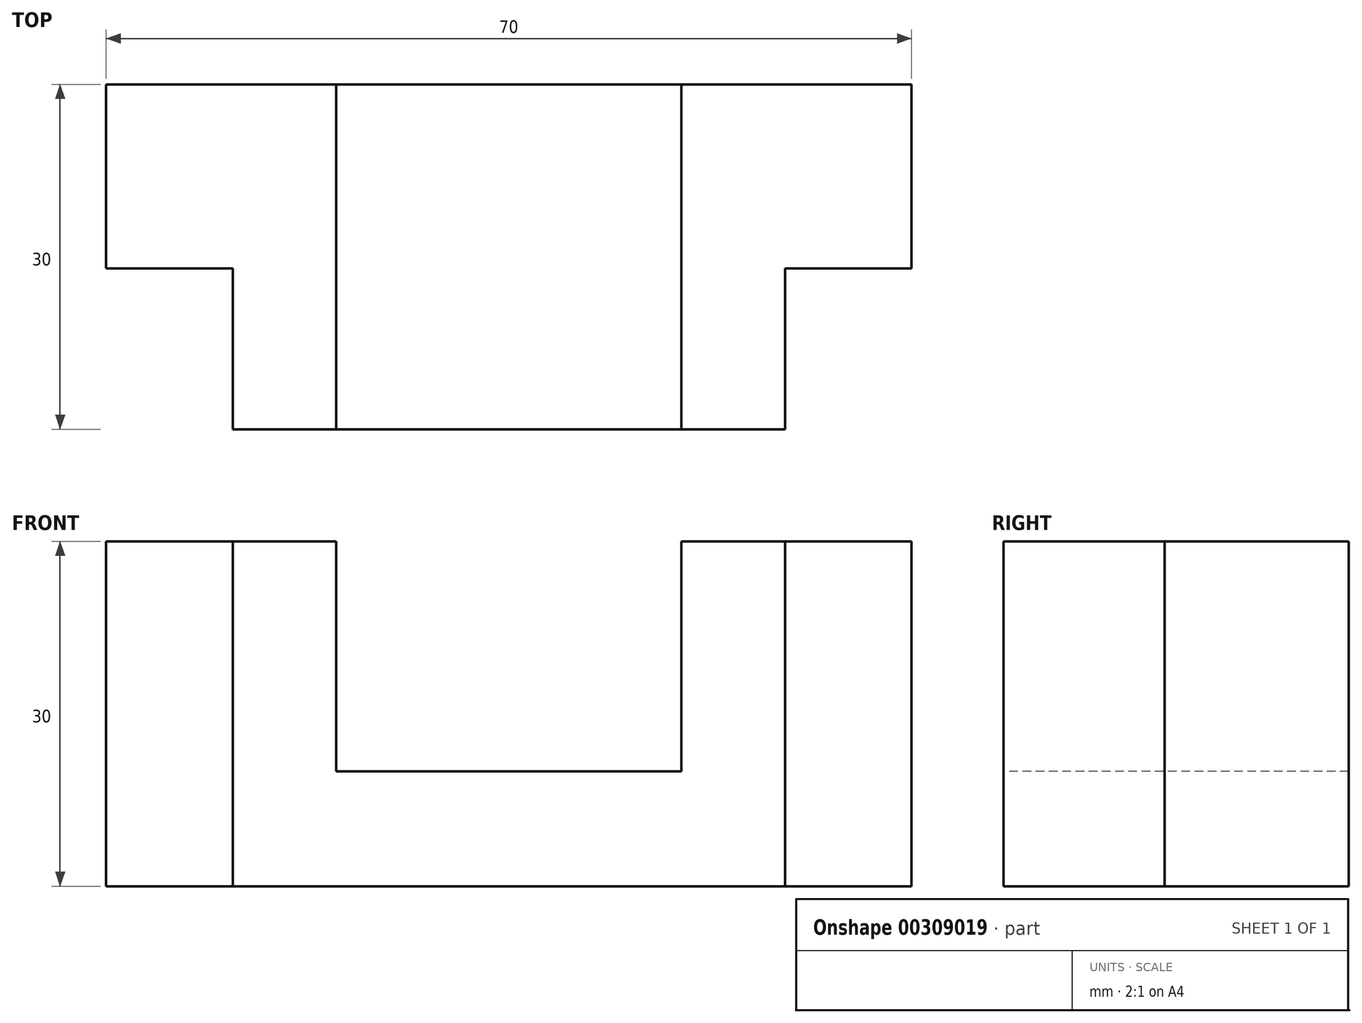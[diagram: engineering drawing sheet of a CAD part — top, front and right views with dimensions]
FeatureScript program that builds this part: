
annotation { "Feature Type Name" : "Feature", "Feature Type Description" : "" }
export const myFeature = defineFeature(function(context is Context, id is Id, definition is map)
    precondition{}
    {
        {
            var Q0;
            Q0=qCreatedBy(makeId("Top.planeOp"),FACE);
            var sketch = newSketch(context, id + "F0", { "sketchPlane" : qUnion([Q0])});
            skLineSegment(sketch, "E0", {"start": v(-35, 16) * mm, "end": v(-35, 0) * mm});
            skLineSegment(sketch, "E1", {"start": v(-24, -14) * mm, "end": v(24, -14) * mm});
            skLineSegment(sketch, "E2", {"start": v(35, 0) * mm, "end": v(35, 16) * mm});
            skLineSegment(sketch, "E3", {"start": v(35, 16) * mm, "end": v(-35, 16) * mm});
            skPoint(sketch, "E4.orphan", {"position": v(-35, 16.86) * mm});
            skLineSegment(sketch, "E5", {"start": v(-35, 0) * mm, "end": v(-24, 0) * mm});
            skLineSegment(sketch, "E6", {"start": v(-24, 0) * mm, "end": v(-24, -14) * mm});
            skLineSegment(sketch, "E7", {"start": v(35, 0) * mm, "end": v(24, 0) * mm});
            skLineSegment(sketch, "E8", {"start": v(24, 0) * mm, "end": v(24, -14) * mm});
            skPoint(sketch, "E9.orphan", {"position": v(-35, -14) * mm});
            skSolve(sketch);
        }
        {
            var Q0;
            Q0=makeQuery(id+"F0.imprint","IMPRINT",FACE,{"disambiguationData":[TD([[makeQuery(id+"F0.imprint","IMPRINT",EDGE,{"derivedFrom":sQuery(id+"F0.wireOp",EDGE,"E0")}),1.0]])]});
            extrude(context, id + "F1", {"entities" : qUnion([Q0]), "depth" : 30 * mm});
        }
        {
            var Q0;
            Q0=makeQuery(id+"F1.opExtrude","SWEPT_FACE",FACE,{"disambiguationData":[OSD([sQuery(id+"F0.wireOp",EDGE,"E1")])]});
            var sketch = newSketch(context, id + "F2", { "sketchPlane" : qUnion([Q0])});
            skPoint(sketch, "E10.end.orphan", {"position": v(-15.27, 0) * mm});
            skLineSegment(sketch, "E11", {"start": v(-15, 30) * mm, "end": v(-15, 10) * mm});
            skLineSegment(sketch, "E12", {"start": v(-15, 10) * mm, "end": v(15, 10) * mm});
            skLineSegment(sketch, "E13", {"start": v(15, 10) * mm, "end": v(15, 30) * mm});
            skSolve(sketch);
        }
        {
            var Q0;
            {var subQ0=sQuery(id+"F2.wireOp",EDGE,"E11");Q0=makeQuery(id+"F2.imprint","IMPRINT",FACE,{"disambiguationData":[TD([[makeQuery(id+"F2.imprint","IMPRINT",EDGE,{"derivedFrom":subQ0}),1.0]])]});}
            extrude(context, id + "F3", {"entities" : qUnion([Q0]), "operationType" : NewBodyOperationType.REMOVE, "oppositeDirection" : true, "depth" : 30 * mm});
        }
    });
